# Revit family: Gira_032030
name_source: partatom
category: Electrical Fixtures
revit_build: Autodesk Revit 2017 (Build: 20160225_1515(x64)
units: mm (PartAtom-declared; Revit-internal decimal feet)

## family parameters
Cut with Voids When Loaded = No
Host = Face
Maintain Annotation Orientation = No
Part Type = Normal
Room Calculation Point = No
Round Connector Dimension = Use Diameter
Shared = No

## types (1)
- Time sw. 2-p 15 min in.sp. WP SM grey
    Assembly arrangement = Basic element
    BIM = https://media.live.bim.site
    BIMSITE_PRODUCT_ID = d637346bdae938aac808b95f1f02415712c8d3c4
    Colour = Grey
    Cost = 0 $
    Default Elevation = 1219 mm
    Description = Time sw.2-p 15min in.sp. WP SM GY Time switch, 2-pole 16 A 250 V~ with inscription space 15 minutes grey Notes : - Different times available on request.
    GTIN = 4010337320302
    HAN = 032030
    Halogen free = No
    HeinzeBIM = https://www.heinze.de
    Manufacturer = Gira
    Material = plastic
    Material quality = Thermoplastic
    Nominal voltage [Volt] Number = 250
    Suitable for degree of protection (IP) = IP44
    Surface protection = Sonstige (*de-DE)
    Time setting [s] = [0:900]
    URL = https://www.gira.de

## geometry (parser evidence)
native form markers: Blend x2, Sweep x14
no freeform markers — native parametric forms only
